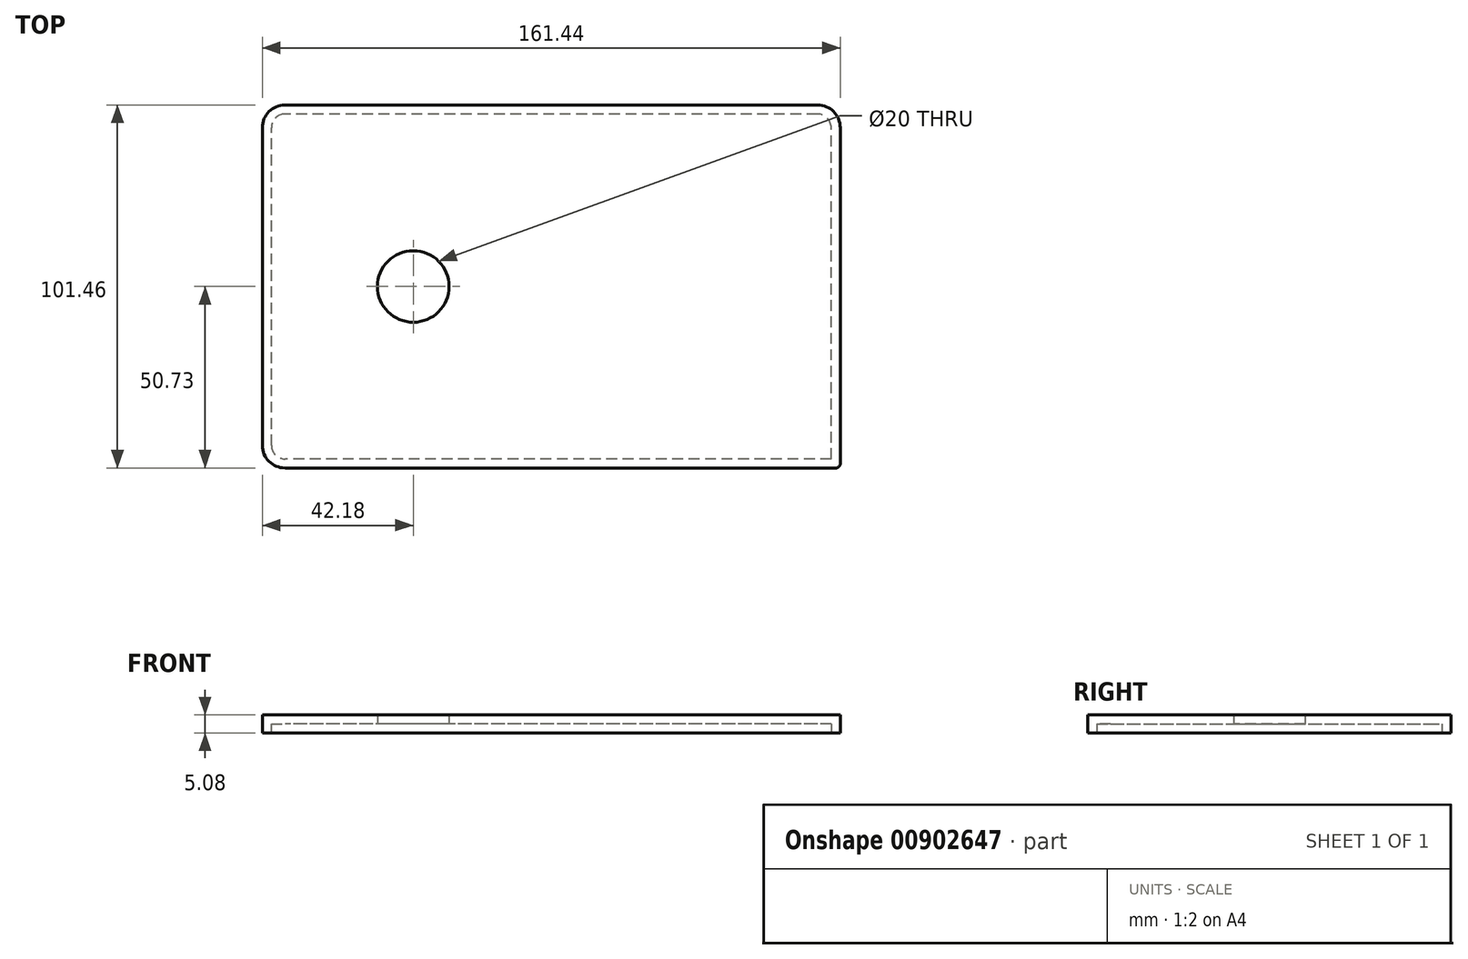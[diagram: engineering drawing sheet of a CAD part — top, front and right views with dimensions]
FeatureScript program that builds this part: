
annotation { "Feature Type Name" : "Feature", "Feature Type Description" : "" }
export const myFeature = defineFeature(function(context is Context, id is Id, definition is map)
    precondition{}
    {
        {
            var Q0;
            Q0=qCreatedBy(makeId("Top.planeOp"),FACE);
            var sketch = newSketch(context, id + "F0", { "sketchPlane" : qUnion([Q0])});
            skLineSegment(sketch, "E0.bottom", {"start": v(79.45, -50.73) * mm, "end": v(-74.37, -50.73) * mm});
            skLineSegment(sketch, "E0.top", {"start": v(74.37, 50.73) * mm, "end": v(-74.37, 50.73) * mm});
            skLineSegment(sketch, "E0.left", {"start": v(80.72, -49.46) * mm, "end": v(80.72, 44.38) * mm});
            skLineSegment(sketch, "E0.right", {"start": v(-80.72, -44.38) * mm, "end": v(-80.72, 44.38) * mm});
            skPoint(sketch, "E0.middle", {"position": v(0, 0) * mm});
            skPoint(sketch, "E1.visualSharp", {"position": v(-80.72, 50.73) * mm});
            skArc(sketch, "E1.filletArc", {"start": v(-74.37, 50.73) * mm, "mid": v(-78.86, 48.87) * mm, "end": v(-80.72, 44.38) * mm});
            skPoint(sketch, "E2.visualSharp", {"position": v(-80.72, -50.73) * mm});
            skArc(sketch, "E2.filletArc", {"start": v(-80.72, -44.38) * mm, "mid": v(-78.86, -48.87) * mm, "end": v(-74.37, -50.73) * mm});
            skPoint(sketch, "E3.visualSharp", {"position": v(80.72, -50.73) * mm});
            skArc(sketch, "E3.filletArc", {"start": v(79.45, -50.73) * mm, "mid": v(80.35, -50.36) * mm, "end": v(80.72, -49.46) * mm});
            skPoint(sketch, "E4.visualSharp", {"position": v(80.72, 50.73) * mm});
            skArc(sketch, "E4.filletArc", {"start": v(80.72, 44.38) * mm, "mid": v(78.86, 48.87) * mm, "end": v(74.37, 50.73) * mm});
            skPoint(sketch, "E5.visualSharp", {"position": v(-70.14, 40.93) * mm});
            skPoint(sketch, "E6.visualSharp", {"position": v(-70.14, -40.93) * mm});
            skPoint(sketch, "E7.visualSharp", {"position": v(70.14, 40.93) * mm});
            skPoint(sketch, "E8.visualSharp", {"position": v(70.14, -40.93) * mm});
            skSolve(sketch);
        }
        {
            var Q0;
            Q0 = qSketchRegion(id + "F0", true);
            extrude(context, id + "F1", {"entities" : qUnion([Q0]), "depth" : 5.08 * mm, "offsetDistance" : 25.4 * mm});
        }
        {
            var Q0;
            Q0=makeQuery(id+"F1.opExtrude","CAP_FACE",FACE,{"disambiguationData":[OSD([sQuery(id+"F0.wireOp",EDGE,"E0.bottom"),sQuery(id+"F0.wireOp",EDGE,"E0.top"),sQuery(id+"F0.wireOp",EDGE,"E0.left"),sQuery(id+"F0.wireOp",EDGE,"E0.right"),sQuery(id+"F0.wireOp",EDGE,"E1.filletArc"),sQuery(id+"F0.wireOp",EDGE,"E2.filletArc"),sQuery(id+"F0.wireOp",EDGE,"E3.filletArc"),sQuery(id+"F0.wireOp",EDGE,"E4.filletArc")])],"isStart":true});
            shell(context, id + "F2", {"entities" : qUnion([Q0]), "thickness" : 2.54 * mm});
        }
        {
            var Q0;
            Q0=qCreatedBy(makeId("Top.planeOp"),FACE);
            var sketch = newSketch(context, id + "F3", { "sketchPlane" : qUnion([Q0])});
            skCircle(sketch, "E9", {"center": v(-38.54, 0) * mm, "radius": 16.73 * mm});
            skSolve(sketch);
        }
        {
            var Q0;
            Q0=sQuery(id+"F3.wireOp",VERTEX,"E9.center");
            var Q1;
            Q1=makeQuery(id+"F1.opExtrude","SWEPT_BODY",BODY,{"disambiguationData":[OSD([sQuery(id+"F0.wireOp",EDGE,"E0.bottom"),sQuery(id+"F0.wireOp",EDGE,"E0.top"),sQuery(id+"F0.wireOp",EDGE,"E0.left"),sQuery(id+"F0.wireOp",EDGE,"E0.right"),sQuery(id+"F0.wireOp",EDGE,"E1.filletArc"),sQuery(id+"F0.wireOp",EDGE,"E2.filletArc"),sQuery(id+"F0.wireOp",EDGE,"E3.filletArc"),sQuery(id+"F0.wireOp",EDGE,"E4.filletArc")])]});
            hole(context, id + "F4", {"style" : HoleStyle.SIMPLE, "endStyle" : HoleEndStyle.THROUGH, "oppositeDirection" : true, "holeDiameter" : 20 * mm, "majorDiameter" : 6.35 * mm, "isTappedThrough" : true, "tappedDepth" : 12.7 * mm, "tapClearance" : 3, "locations" : qUnion([Q0]), "scope" : qUnion([Q1])});
        }
    });
